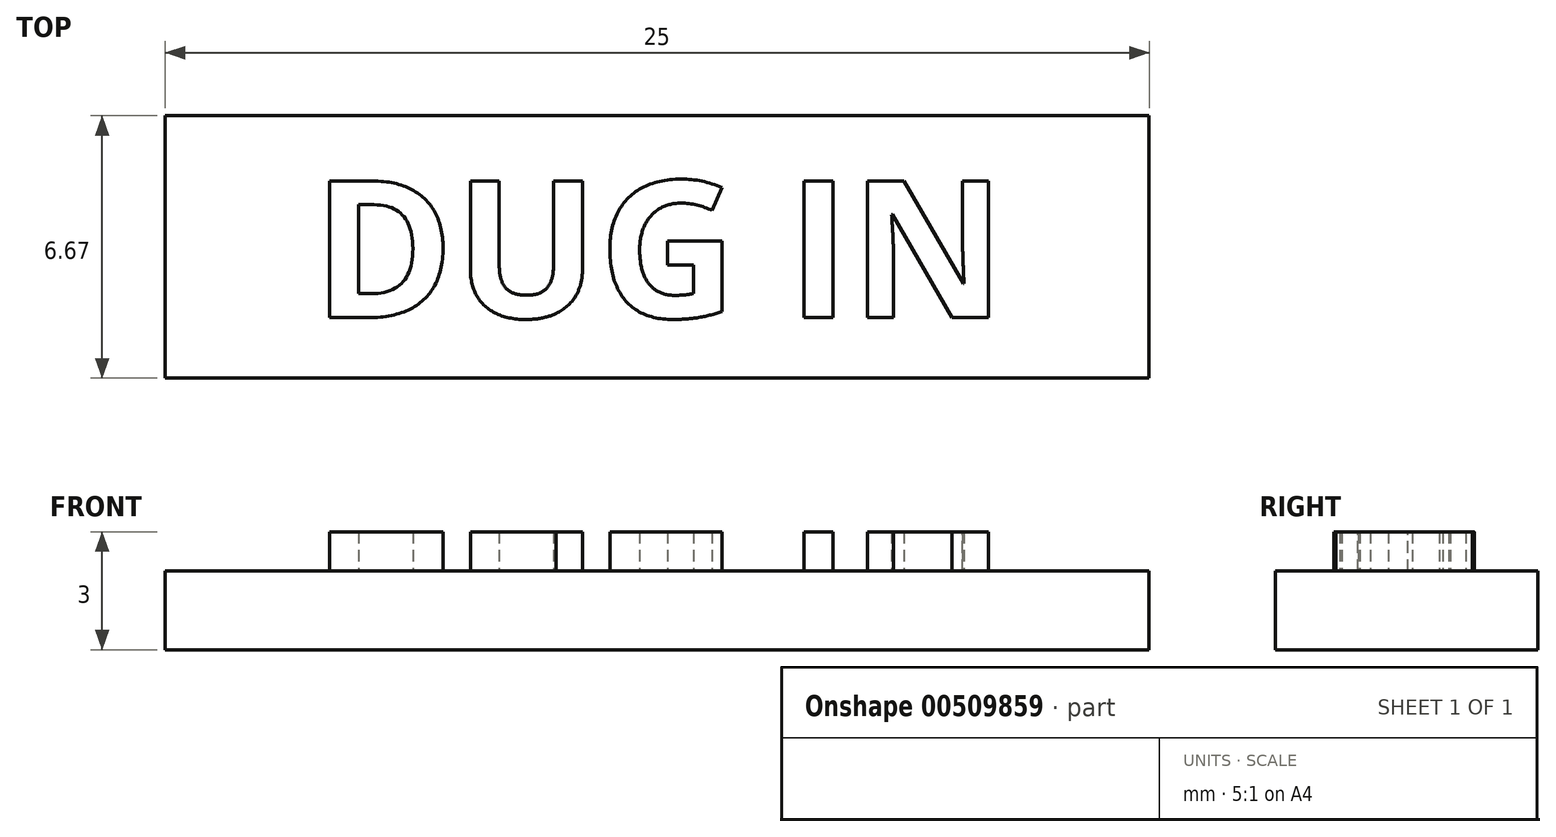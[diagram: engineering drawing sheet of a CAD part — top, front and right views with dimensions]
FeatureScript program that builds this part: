
annotation { "Feature Type Name" : "Feature", "Feature Type Description" : "" }
export const myFeature = defineFeature(function(context is Context, id is Id, definition is map)
    precondition{}
    {
        {
            var Q0;
            Q0=qCreatedBy(makeId("Top.planeOp"),FACE);
            var sketch = newSketch(context, id + "F0", { "sketchPlane" : qUnion([Q0])});
            skLineSegment(sketch, "E0.bottom", {"start": v(-50.71, 29.76) * mm, "end": v(-25.71, 29.76) * mm});
            skLineSegment(sketch, "E0.top", {"start": v(-50.71, 23.1) * mm, "end": v(-25.71, 23.1) * mm});
            skLineSegment(sketch, "E0.left", {"start": v(-50.71, 29.76) * mm, "end": v(-50.71, 23.1) * mm});
            skLineSegment(sketch, "E0.right", {"start": v(-25.71, 29.76) * mm, "end": v(-25.71, 23.1) * mm});
            skSolve(sketch);
        }
        {
            var Q0;
            Q0=qSketchRegion(id+"F0",true);
            extrude(context, id + "F1", {"entities" : qUnion([Q0]), "depth" : 2 * mm, "offsetDistance" : 25 * mm});
        }
        {
            var Q0;
            Q0=makeQuery(id+"F1.opExtrude","CAP_FACE",FACE,{"disambiguationData":[OSD([sQuery(id+"F0.wireOp",EDGE,"E0.bottom"),sQuery(id+"F0.wireOp",EDGE,"E0.top"),sQuery(id+"F0.wireOp",EDGE,"E0.left"),sQuery(id+"F0.wireOp",EDGE,"E0.right")])],"isStart":false});
            var sketch = newSketch(context, id + "F2", { "sketchPlane" : qUnion([Q0])});
            skText(sketch, "E1", { "text": "DUG IN", "fontName": "OpenSans-Bold.ttf"});
            skPoint(sketch, "E2.startSnap0", {"position": v(-38.21, 29.76) * mm});
            const initialGuessF2  = {"E1": [-0.04697, 0.02463, 1, 0, 0.0035]};
            skSetInitialGuess(sketch, initialGuessF2);
            skSolve(sketch);
        }
        {
            var Q0;
            Q0 = qSketchRegion(id + "F2", true);
            extrude(context, id + "F3", {"entities" : qUnion([Q0]), "operationType" : NewBodyOperationType.ADD, "depth" : 1 * mm, "offsetDistance" : 25 * mm});
        }
    });
